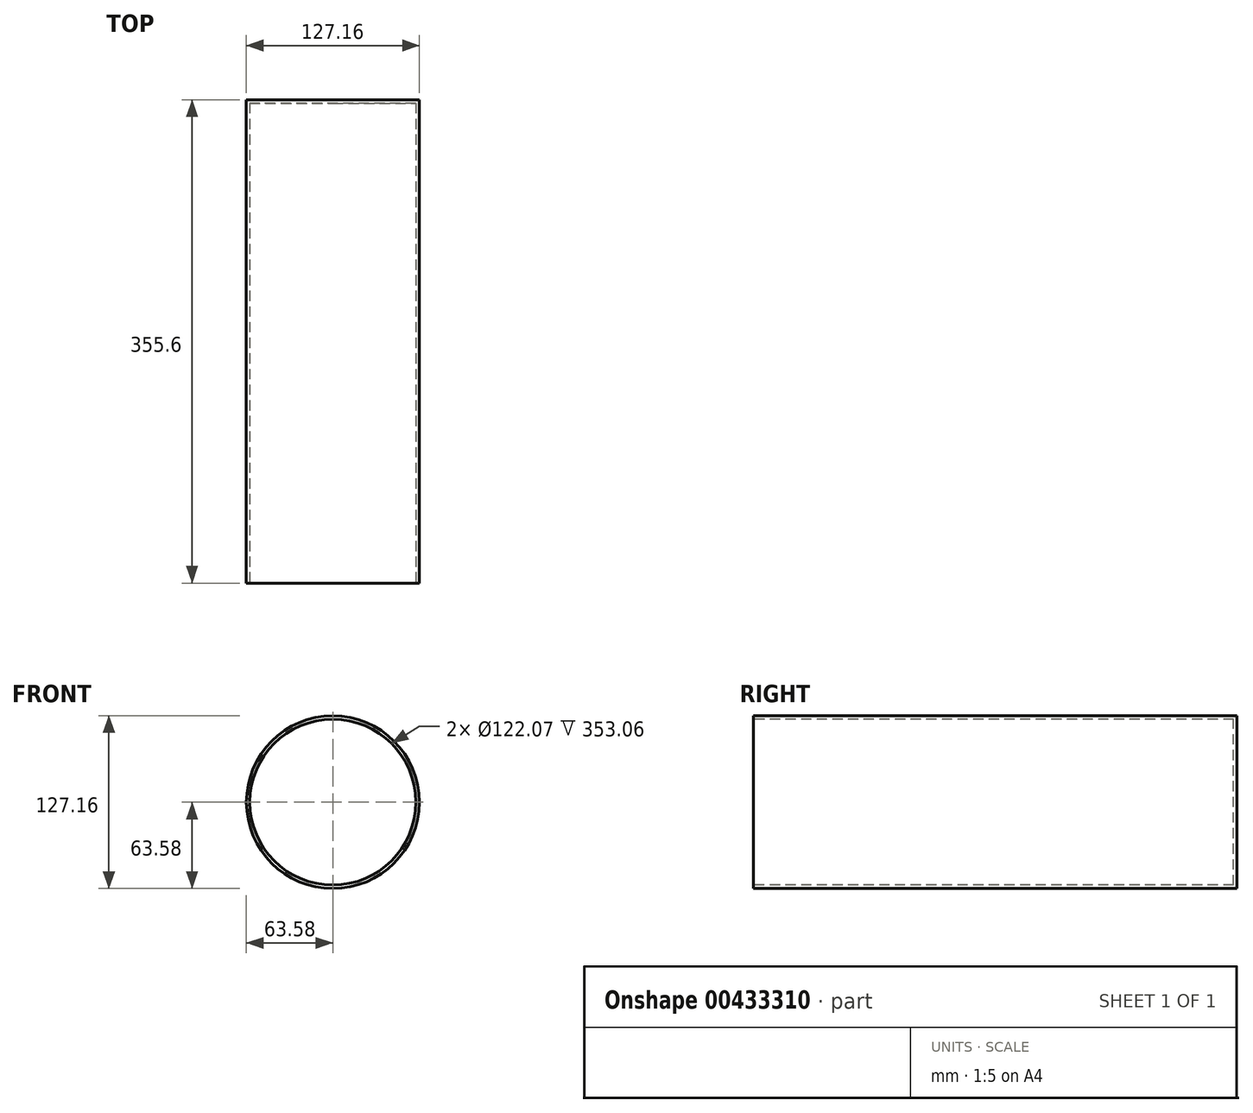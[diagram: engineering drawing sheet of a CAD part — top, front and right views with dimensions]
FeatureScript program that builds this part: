
annotation { "Feature Type Name" : "Feature", "Feature Type Description" : "" }
export const myFeature = defineFeature(function(context is Context, id is Id, definition is map)
    precondition{}
    {
        {
            var Q0;
            Q0=qCreatedBy(makeId("Front.planeOp"),FACE);
            var sketch = newSketch(context, id + "F0", { "sketchPlane" : qUnion([Q0])});
            skCircle(sketch, "E0", {"center": v(0, 0) * mm, "radius": 63.58 * mm});
            skSolve(sketch);
        }
        {
            var Q0;
            Q0 = qSketchRegion(id + "F0", true);
            extrude(context, id + "F1", {"entities" : qUnion([Q0]), "oppositeDirection" : true, "depth" : 355.6 * mm});
        }
        {
            var Q0;
            Q0=makeQuery(id+"F1.opExtrude","CAP_FACE",FACE,{"disambiguationData":[OSD([sQuery(id+"F0.wireOp",EDGE,"E0")])],"isStart":true});
            shell(context, id + "F2", {"entities" : qUnion([Q0]), "thickness" : 2.54 * mm});
        }
    });
